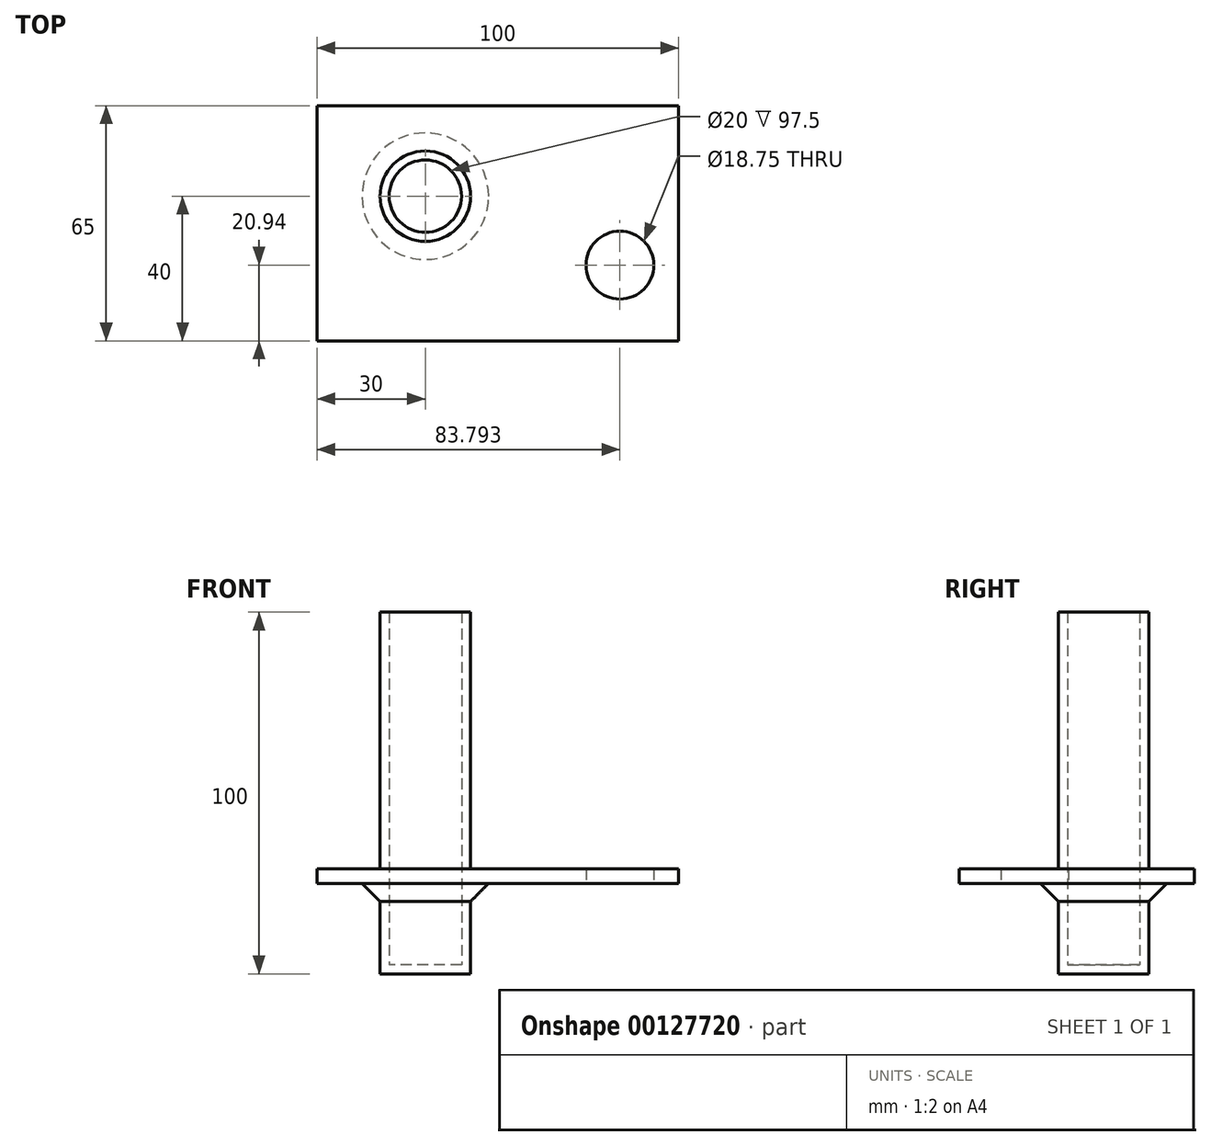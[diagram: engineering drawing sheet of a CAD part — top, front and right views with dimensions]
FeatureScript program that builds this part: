
annotation { "Feature Type Name" : "Feature", "Feature Type Description" : "" }
export const myFeature = defineFeature(function(context is Context, id is Id, definition is map)
    precondition{}
    {
        {
            var Q0;
            Q0=qCreatedBy(makeId("Top.planeOp"),FACE);
            var sketch = newSketch(context, id + "F0", { "sketchPlane" : qUnion([Q0])});
            skCircle(sketch, "E0", {"center": v(0, 0) * mm, "radius": 12.5 * mm});
            skSolve(sketch);
        }
        {
            var Q0;
            Q0=makeQuery(id+"F0.imprint","IMPRINT",FACE,{"disambiguationData":[TD([[makeQuery(id+"F0.imprint","IMPRINT",EDGE,{"derivedFrom":sQuery(id+"F0.wireOp",EDGE,"E0")}),1.0]])]});
            extrude(context, id + "F1", {"entities" : qUnion([Q0]), "depth" : 100 * mm});
        }
        {
            var Q0;
            Q0=makeQuery(id+"F1.opExtrude","CAP_FACE",FACE,{"disambiguationData":[OSD([sQuery(id+"F0.wireOp",EDGE,"E0")])],"isStart":false});
            shell(context, id + "F2", {"entities" : qUnion([Q0]), "thickness" : 2.5 * mm});
        }
        {
            var Q0;
            Q0=qCreatedBy(makeId("Top.planeOp"),FACE);
            cPlane(context, id + "F3", {"entities" : qUnion([Q0]), "cplaneType" : CPlaneType.OFFSET, "offset" : 25 * mm, "width" : 150 * mm, "height" : 150 * mm});
        }
        {
            var Q0;
            Q0=qCreatedBy(id+"F3.planeOp",FACE);
            var sketch = newSketch(context, id + "F4", { "sketchPlane" : qUnion([Q0])});
            skCircle(sketch, "E1", {"center": v(0, 0) * mm, "radius": 12.5 * mm});
            skLineSegment(sketch, "E2.bottom", {"start": v(-30, -40) * mm, "end": v(70, -40) * mm});
            skLineSegment(sketch, "E2.top", {"start": v(-30, 25) * mm, "end": v(70, 25) * mm});
            skLineSegment(sketch, "E2.left", {"start": v(-30, -40) * mm, "end": v(-30, 25) * mm});
            skLineSegment(sketch, "E2.right", {"start": v(70, -40) * mm, "end": v(70, 25) * mm});
            skCircle(sketch, "E3", {"center": v(53.8, -19.06) * mm, "radius": 9.38 * mm});
            skSolve(sketch);
        }
        {
            var Q0;
            Q0=makeQuery(id+"F4.imprint","IMPRINT",FACE,{"disambiguationData":[TD([[makeQuery(id+"F4.imprint","IMPRINT",EDGE,{"derivedFrom":sQuery(id+"F4.wireOp",EDGE,"E1")}),-1.0]])]});
            extrude(context, id + "F5", {"entities" : qUnion([Q0]), "operationType" : NewBodyOperationType.ADD, "depth" : 4 * mm});
        }
        {
            var Q0;
            Q0=makeQuery(id+"F5.opExtrude","CAP_EDGE",EDGE,{"disambiguationData":[OSD([sQuery(id+"F4.wireOp",EDGE,"E1")])],"isStart":false});
            var Q1;
            Q1=makeQuery(id+"F5.opExtrude","CAP_EDGE",EDGE,{"disambiguationData":[OSD([sQuery(id+"F4.wireOp",EDGE,"E1")])],"isStart":true});
            chamfer(context, id + "F6", {"entities" : qUnion([Q0, Q1]), "width" : 5 * mm, "tangentPropagation" : true});
        }
    });
